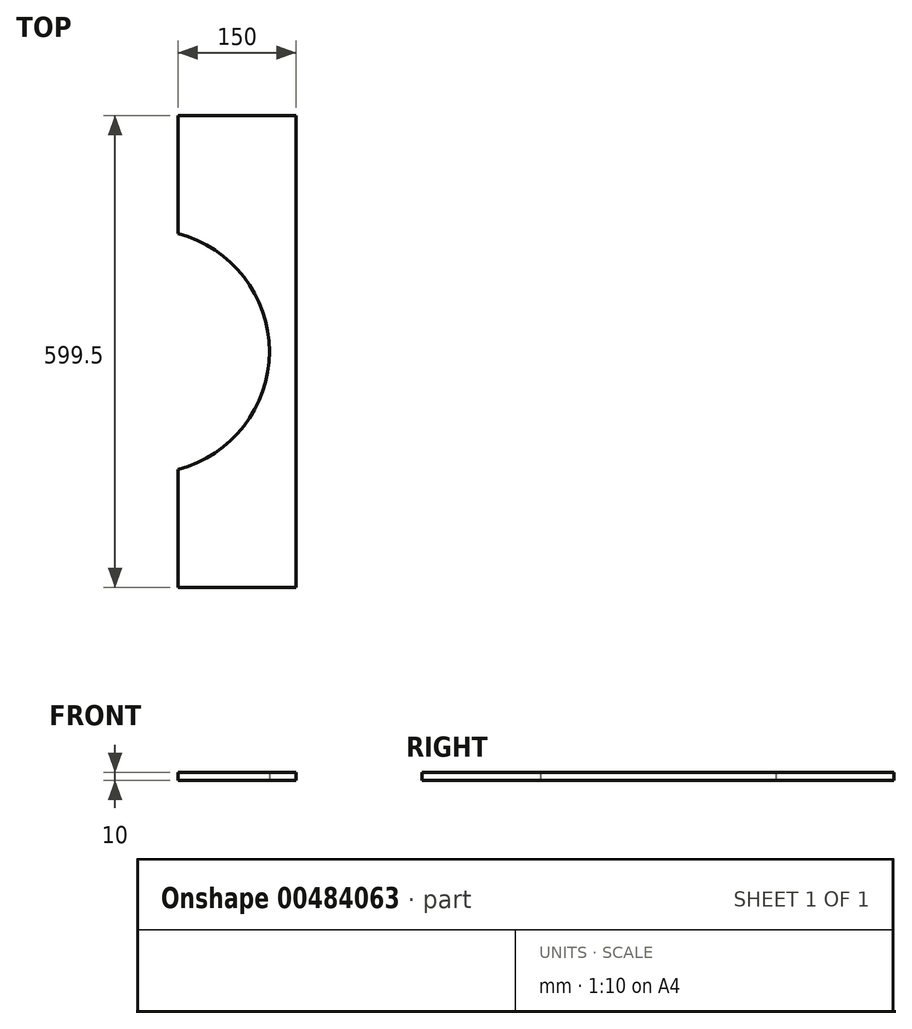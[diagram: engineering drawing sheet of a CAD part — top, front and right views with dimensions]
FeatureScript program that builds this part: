
annotation { "Feature Type Name" : "Feature", "Feature Type Description" : "" }
export const myFeature = defineFeature(function(context is Context, id is Id, definition is map)
    precondition{}
    {
        {
            var Q0;
            Q0=qCreatedBy(makeId("Top.planeOp"),FACE);
            var sketch = newSketch(context, id + "F0", { "sketchPlane" : qUnion([Q0])});
            skLineSegment(sketch, "E0", {"start": v(40, -149.75) * mm, "end": v(40, -299.75) * mm});
            skLineSegment(sketch, "E1", {"start": v(40, 149.75) * mm, "end": v(40, 299.75) * mm});
            skLineSegment(sketch, "E2", {"start": v(40, -299.75) * mm, "end": v(190, -299.75) * mm});
            skLineSegment(sketch, "E3", {"start": v(190, -299.75) * mm, "end": v(190, 299.75) * mm});
            skLineSegment(sketch, "E4", {"start": v(190, 299.75) * mm, "end": v(40, 299.75) * mm});
            skArc(sketch, "E5", {"start": v(40, -149.75) * mm, "mid": v(155.88, 0) * mm, "end": v(40, 149.75) * mm});
            skSolve(sketch);
        }
        {
            var Q0;
            Q0=qSketchRegion(id+"F0",true);
            extrude(context, id + "F1", {"entities" : qUnion([Q0]), "depth" : 10 * mm, "offsetDistance" : 25 * mm});
        }
        {
            var Q0;
            Q0 = qSketchRegion(id + "F0", true);
            extrude(context, id + "F2", {"entities" : qUnion([Q0]), "operationType" : NewBodyOperationType.ADD, "depth" : 10 * mm, "offsetDistance" : 25 * mm});
        }
    });
